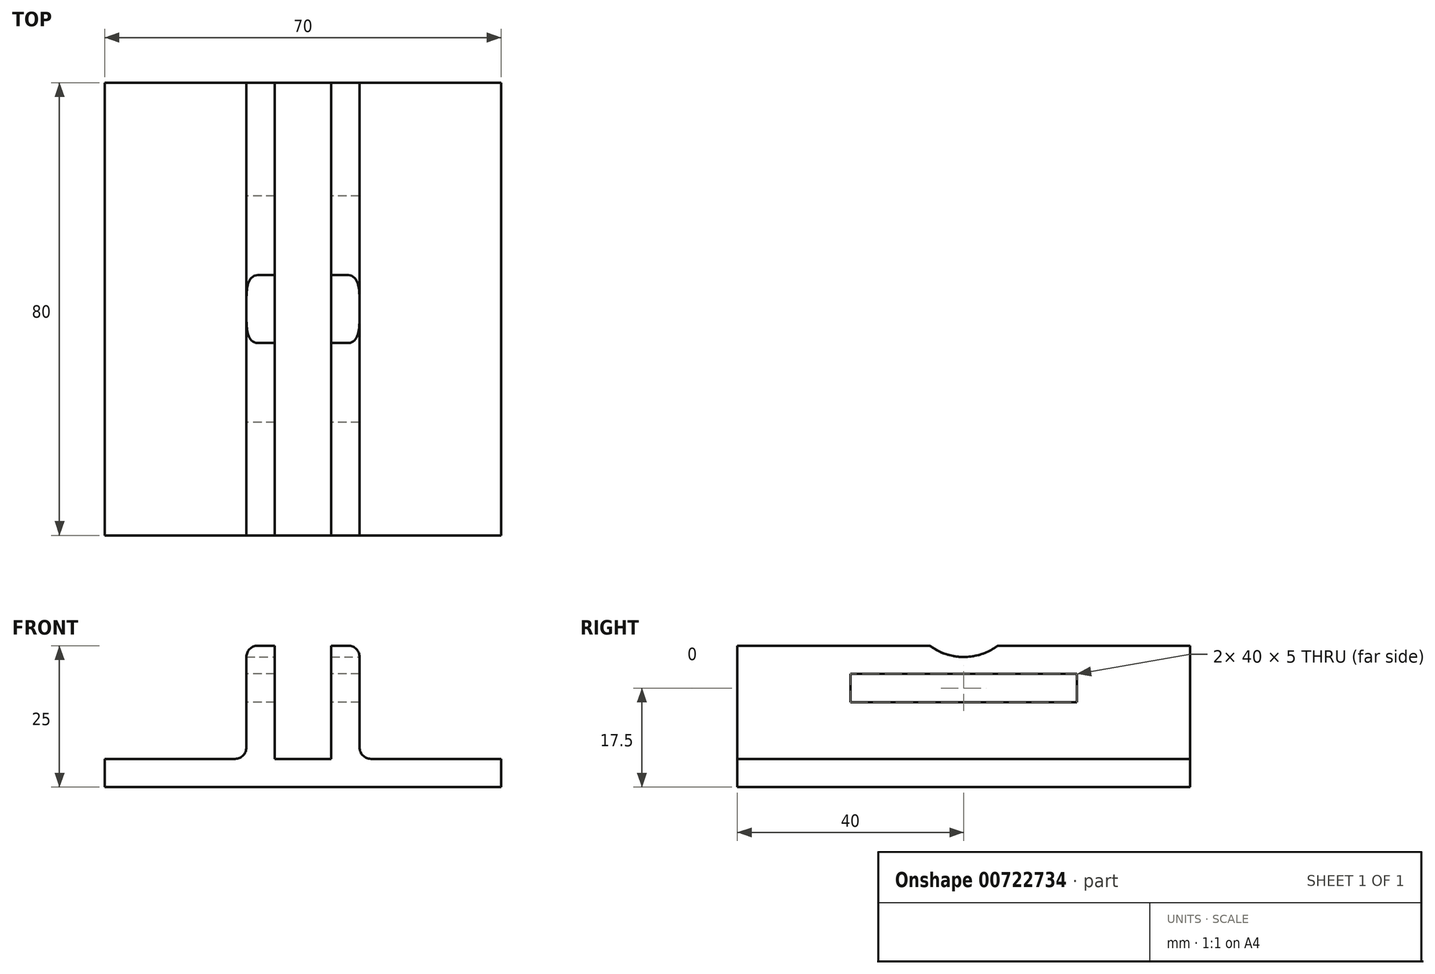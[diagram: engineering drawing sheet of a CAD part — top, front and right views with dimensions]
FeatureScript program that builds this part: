
annotation { "Feature Type Name" : "Feature", "Feature Type Description" : "" }
export const myFeature = defineFeature(function(context is Context, id is Id, definition is map)
    precondition{}
    {
        {
            var Q0;
            Q0=qCreatedBy(makeId("Front.planeOp"),FACE);
            var sketch = newSketch(context, id + "F0", { "sketchPlane" : qUnion([Q0])});
            skLineSegment(sketch, "E0.bottom", {"start": v(0, 0) * mm, "end": v(-10, 0) * mm, "construction": true});
            skLineSegment(sketch, "E0.top", {"start": v(0, 20) * mm, "end": v(-10, 20) * mm, "construction": true});
            skLineSegment(sketch, "E0.left", {"start": v(0, 0) * mm, "end": v(0, 20) * mm, "construction": true});
            skLineSegment(sketch, "E0.right", {"start": v(-10, 0) * mm, "end": v(-10, 20) * mm, "construction": true});
            skLineSegment(sketch, "E1.bottom", {"start": v(-10, 20) * mm, "end": v(-15, 20) * mm});
            skLineSegment(sketch, "E1.top", {"start": v(-10, 0) * mm, "end": v(-15, 0) * mm, "construction": true});
            skLineSegment(sketch, "E1.left", {"start": v(-10, 20) * mm, "end": v(-10, 0) * mm});
            skLineSegment(sketch, "E1.right", {"start": v(-15, 20) * mm, "end": v(-15, 0) * mm});
            skLineSegment(sketch, "E2.bottom", {"start": v(0, 20) * mm, "end": v(5, 20) * mm});
            skLineSegment(sketch, "E2.top", {"start": v(0, 0) * mm, "end": v(5, 0) * mm});
            skLineSegment(sketch, "E2.left", {"start": v(0, 20) * mm, "end": v(0, 0) * mm});
            skLineSegment(sketch, "E2.right", {"start": v(5, 20) * mm, "end": v(5, 0) * mm});
            skLineSegment(sketch, "E3.bottom", {"start": v(0, 0) * mm, "end": v(-40, 0) * mm});
            skLineSegment(sketch, "E3.top", {"start": v(0, -5) * mm, "end": v(-40, -5) * mm});
            skLineSegment(sketch, "E3.left", {"start": v(0, 0) * mm, "end": v(0, -5) * mm});
            skLineSegment(sketch, "E3.right", {"start": v(-40, 0) * mm, "end": v(-40, -5) * mm});
            skLineSegment(sketch, "E4.bottom", {"start": v(0, 0) * mm, "end": v(30, 0) * mm});
            skLineSegment(sketch, "E4.top", {"start": v(0, -5) * mm, "end": v(30, -5) * mm});
            skLineSegment(sketch, "E4.right", {"start": v(30, 0) * mm, "end": v(30, -5) * mm});
            skSolve(sketch);
        }
        {
            var Q0;
            Q0 = qSketchRegion(id + "F0", true);
            extrude(context, id + "F1", {"entities" : qUnion([Q0]), "depth" : 80 * mm, "offsetDistance" : 25 * mm, "symmetric" : true});
        }
        {
            var Q0;
            Q0=makeQuery(id+"F1.opExtrude","SWEPT_EDGE",EDGE,{"disambiguationData":[OSD([sQuery(id+"F0.wireOp",EDGE,"E2.right"),sQuery(id+"F0.wireOp",EDGE,"E4.bottom")])]});
            var Q1;
            Q1=makeQuery(id+"F1.opExtrude","SWEPT_EDGE",EDGE,{"disambiguationData":[OSD([sQuery(id+"F0.wireOp",EDGE,"E1.right"),sQuery(id+"F0.wireOp",EDGE,"E3.bottom")])]});
            fillet(context, id + "F2", {"entities" : qUnion([Q0, Q1]), "radius" : 2 * mm, "tangentPropagation" : true, "allowEdgeOverflow" : false});
        }
        {
            var Q0;
            Q0=makeQuery(id+"F1.opExtrude","SWEPT_EDGE",EDGE,{"disambiguationData":[OSD([sQuery(id+"F0.wireOp",EDGE,"E1.bottom"),sQuery(id+"F0.wireOp",EDGE,"E1.right")])]});
            var Q1;
            Q1=makeQuery(id+"F1.opExtrude","SWEPT_EDGE",EDGE,{"disambiguationData":[OSD([sQuery(id+"F0.wireOp",EDGE,"E2.bottom"),sQuery(id+"F0.wireOp",EDGE,"E2.right")])]});
            fillet(context, id + "F3", {"entities" : qUnion([Q0, Q1]), "radius" : 2 * mm, "tangentPropagation" : true, "allowEdgeOverflow" : false});
        }
        {
            var Q0;
            Q0=makeQuery(id+"F1.opExtrude","SWEPT_FACE",FACE,{"disambiguationData":[OSD([sQuery(id+"F0.wireOp",EDGE,"E1.right")])]});
            var sketch = newSketch(context, id + "F4", { "sketchPlane" : qUnion([Q0])});
            skLineSegment(sketch, "E5", {"start": v(-40, 0) * mm, "end": v(-20, 0) * mm, "construction": true});
            skLineSegment(sketch, "E6", {"start": v(-20, 0) * mm, "end": v(-20, 10) * mm, "construction": true});
            skLineSegment(sketch, "E7.bottom", {"start": v(-20, 10) * mm, "end": v(20, 10) * mm});
            skLineSegment(sketch, "E7.top", {"start": v(-20, 15) * mm, "end": v(20, 15) * mm});
            skLineSegment(sketch, "E7.left", {"start": v(-20, 10) * mm, "end": v(-20, 15) * mm});
            skLineSegment(sketch, "E7.right", {"start": v(20, 10) * mm, "end": v(20, 15) * mm});
            skSolve(sketch);
        }
        {
            var Q0;
            Q0 = qSketchRegion(id + "F4", true);
            extrude(context, id + "F5", {"entities" : qUnion([Q0]), "operationType" : NewBodyOperationType.REMOVE, "oppositeDirection" : true, "depth" : 25 * mm, "offsetDistance" : 25 * mm});
        }
        {
            var Q0;
            Q0=makeQuery(id+"F1.opExtrude","SWEPT_FACE",FACE,{"disambiguationData":[OSD([sQuery(id+"F0.wireOp",EDGE,"E2.right")])]});
            var sketch = newSketch(context, id + "F6", { "sketchPlane" : qUnion([Q0])});
            skLineSegment(sketch, "E8", {"start": v(0, 0) * mm, "end": v(0, 28) * mm, "construction": true});
            skCircle(sketch, "E9", {"center": v(0, 28) * mm, "radius": 10 * mm});
            skSolve(sketch);
        }
        {
            var Q0;
            Q0 = qSketchRegion(id + "F6", true);
            extrude(context, id + "F7", {"entities" : qUnion([Q0]), "operationType" : NewBodyOperationType.REMOVE, "oppositeDirection" : true, "depth" : 25 * mm, "offsetDistance" : 25 * mm});
        }
    });
